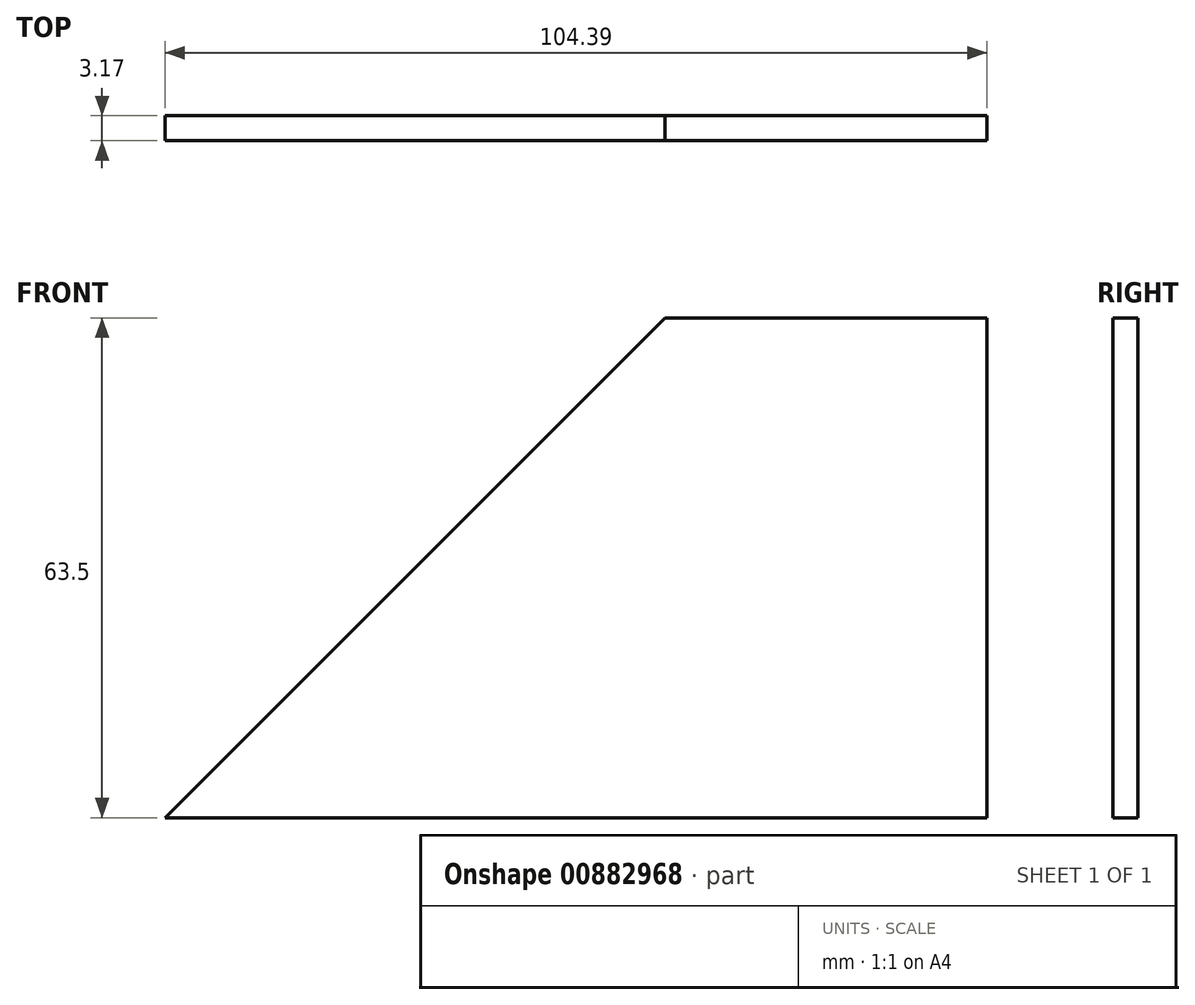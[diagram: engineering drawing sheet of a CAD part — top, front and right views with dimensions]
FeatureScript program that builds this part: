
annotation { "Feature Type Name" : "Feature", "Feature Type Description" : "" }
export const myFeature = defineFeature(function(context is Context, id is Id, definition is map)
    precondition{}
    {
        {
            var Q0;
            Q0=qCreatedBy(makeId("Front.planeOp"),FACE);
            var sketch = newSketch(context, id + "F0", { "sketchPlane" : qUnion([Q0])});
            skLineSegment(sketch, "E0", {"start": v(0, 0) * mm, "end": v(0, 63.5) * mm});
            skLineSegment(sketch, "E1", {"start": v(0, 63.5) * mm, "end": v(-40.89, 63.5) * mm});
            skLineSegment(sketch, "E2", {"start": v(-40.89, 63.5) * mm, "end": v(-104.39, 0) * mm});
            skLineSegment(sketch, "E3", {"start": v(-104.39, 0) * mm, "end": v(0, 0) * mm});
            skSolve(sketch);
        }
        {
            var Q0;
            Q0 = qSketchRegion(id + "F0", true);
            extrude(context, id + "F1", {"entities" : qUnion([Q0]), "depth" : 3.17 * mm, "offsetDistance" : 25.4 * mm});
        }
    });
